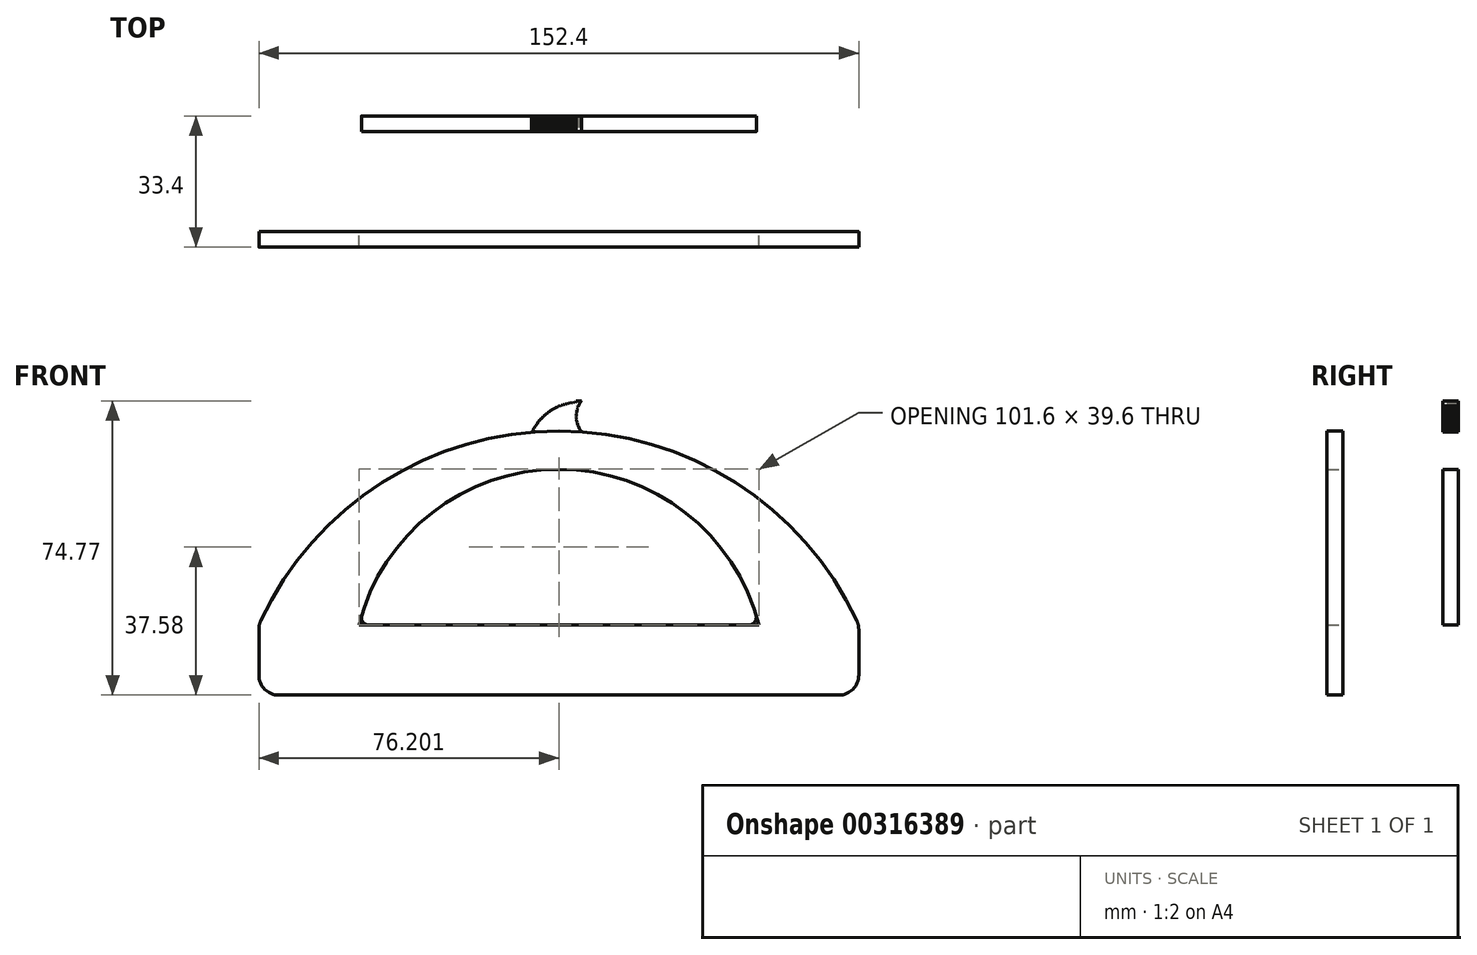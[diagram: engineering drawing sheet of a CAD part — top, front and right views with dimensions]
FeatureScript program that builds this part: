
annotation { "Feature Type Name" : "Feature", "Feature Type Description" : "" }
export const myFeature = defineFeature(function(context is Context, id is Id, definition is map)
    precondition{}
    {
        {
            var Q0;
            Q0=qCreatedBy(makeId("Front.planeOp"),FACE);
            var sketch = newSketch(context, id + "F0", { "sketchPlane" : qUnion([Q0])});
            skLineSegment(sketch, "E0.bottom", {"start": v(-70.76, 0) * mm, "end": v(30.84, 0) * mm});
            skLineSegment(sketch, "E0.top", {"start": v(-70.76, -17.78) * mm, "end": v(30.84, -17.78) * mm});
            skLineSegment(sketch, "E0.left", {"start": v(-70.76, 0) * mm, "end": v(-70.76, -17.78) * mm});
            skLineSegment(sketch, "E0.right", {"start": v(30.84, 0) * mm, "end": v(30.84, -17.78) * mm});
            skLineSegment(sketch, "E1", {"start": v(-19.96, 0) * mm, "end": v(-19.96, 49.32) * mm, "construction": true});
            skLineSegment(sketch, "E2", {"start": v(-70.76, 0) * mm, "end": v(-96.16, 0) * mm});
            skLineSegment(sketch, "E3", {"start": v(30.84, 0) * mm, "end": v(56.24, 0) * mm});
            skLineSegment(sketch, "E4", {"start": v(-96.16, 0) * mm, "end": v(-96.16, -17.78) * mm});
            skLineSegment(sketch, "E5", {"start": v(-96.16, -17.78) * mm, "end": v(-70.76, -17.78) * mm});
            skLineSegment(sketch, "E6", {"start": v(30.84, -17.78) * mm, "end": v(56.24, -17.78) * mm});
            skLineSegment(sketch, "E7", {"start": v(56.24, 0) * mm, "end": v(56.24, -17.78) * mm});
            skArc(sketch, "E8", {"start": v(56.24, 0) * mm, "mid": v(-19.96, 49.32) * mm, "end": v(-96.16, 0) * mm});
            skArc(sketch, "E9", {"start": v(30.84, 0) * mm, "mid": v(-19.96, 39.6) * mm, "end": v(-70.76, 0) * mm});
            skSolve(sketch);
        }
        {
            var Q0;
            Q0=makeQuery(id+"F0.imprint","IMPRINT",FACE,{"disambiguationData":[TD([[makeQuery(id+"F0.imprint","IMPRINT",EDGE,{"derivedFrom":sQuery(id+"F0.wireOp",EDGE,"E2")}),-1.0]])]});
            var Q1;
            Q1=makeQuery(id+"F0.imprint","IMPRINT",FACE,{"disambiguationData":[TD([[makeQuery(id+"F0.imprint","IMPRINT",EDGE,{"derivedFrom":sQuery(id+"F0.wireOp",EDGE,"E0.left")}),-1.0]])]});
            var Q2;
            Q2=makeQuery(id+"F0.imprint","IMPRINT",FACE,{"disambiguationData":[TD([[makeQuery(id+"F0.imprint","IMPRINT",EDGE,{"derivedFrom":sQuery(id+"F0.wireOp",EDGE,"E0.bottom")}),-1.0]])]});
            var Q3;
            Q3=makeQuery(id+"F0.imprint","IMPRINT",FACE,{"disambiguationData":[TD([[makeQuery(id+"F0.imprint","IMPRINT",EDGE,{"derivedFrom":sQuery(id+"F0.wireOp",EDGE,"E0.right")}),1.0]])]});
            extrude(context, id + "F1", {"entities" : qUnion([Q0, Q1, Q2, Q3]), "depth" : 4 * mm});
        }
        {
            var Q0;
            Q0=makeQuery(id+"F1.opExtrude","SWEPT_EDGE",EDGE,{"disambiguationData":[OSD([sQuery(id+"F0.wireOp",EDGE,"E4"),sQuery(id+"F0.wireOp",EDGE,"E5")])]});
            var Q1;
            Q1=makeQuery(id+"F1.opExtrude","SWEPT_EDGE",EDGE,{"disambiguationData":[OSD([sQuery(id+"F0.wireOp",EDGE,"E2"),sQuery(id+"F0.wireOp",EDGE,"E4"),sQuery(id+"F0.wireOp",EDGE,"E8")])]});
            var Q2;
            Q2=makeQuery(id+"F1.opExtrude","SWEPT_EDGE",EDGE,{"disambiguationData":[OSD([sQuery(id+"F0.wireOp",EDGE,"E3"),sQuery(id+"F0.wireOp",EDGE,"E7"),sQuery(id+"F0.wireOp",EDGE,"E8")])]});
            var Q3;
            Q3=makeQuery(id+"F1.opExtrude","SWEPT_EDGE",EDGE,{"disambiguationData":[OSD([sQuery(id+"F0.wireOp",EDGE,"E6"),sQuery(id+"F0.wireOp",EDGE,"E7")])]});
            fillet(context, id + "F2", {"entities" : qUnion([Q0, Q1, Q2, Q3]), "radius" : 5.08 * mm, "tangentPropagation" : true, "allowEdgeOverflow" : false});
        }
        {
            var Q0;
            Q0=makeQuery(id+"F1.opExtrude","CAP_FACE",FACE,{"disambiguationData":[OSD([sQuery(id+"F0.wireOp",EDGE,"E0.bottom"),sQuery(id+"F0.wireOp",EDGE,"E0.top"),sQuery(id+"F0.wireOp",EDGE,"E4"),sQuery(id+"F0.wireOp",EDGE,"E5"),sQuery(id+"F0.wireOp",EDGE,"E6"),sQuery(id+"F0.wireOp",EDGE,"E7"),sQuery(id+"F0.wireOp",EDGE,"E8"),sQuery(id+"F0.wireOp",EDGE,"E9")])],"isStart":true});
            cPlane(context, id + "F3", {"entities" : qUnion([Q0]), "cplaneType" : CPlaneType.OFFSET, "offset" : 25.4 * mm, "width" : 152.4 * mm, "height" : 152.4 * mm});
        }
        {
            var Q0;
            Q0=qCreatedBy(id+"F3.planeOp",FACE);
            var sketch = newSketch(context, id + "F4", { "sketchPlane" : qUnion([Q0])});
            skArc(sketch, "E10.0", {"start": v(-55.77, 1.04) * mm, "mid": v(19.96, 49.32) * mm, "end": v(95.68, 1.04) * mm});
            skArc(sketch, "E11.0", {"start": v(-30.84, 0) * mm, "mid": v(19.96, 39.6) * mm, "end": v(70.76, 0) * mm});
            skLineSegment(sketch, "E12.0", {"start": v(70.76, 0) * mm, "end": v(-30.84, 0) * mm});
            skLineSegment(sketch, "E13.0", {"start": v(91.08, -17.78) * mm, "end": v(-51.16, -17.78) * mm});
            skLineSegment(sketch, "E14.0", {"start": v(-56.24, -1.1) * mm, "end": v(-56.24, -12.7) * mm});
            skArc(sketch, "E15.0", {"start": v(-56.24, -12.7) * mm, "mid": v(-54.75, -16.3) * mm, "end": v(-51.16, -17.78) * mm});
            skArc(sketch, "E16.0", {"start": v(91.08, -17.78) * mm, "mid": v(94.67, -16.3) * mm, "end": v(96.16, -12.7) * mm});
            skLineSegment(sketch, "E17.0", {"start": v(96.16, -1.1) * mm, "end": v(96.16, -12.7) * mm});
            skArc(sketch, "E18.0", {"start": v(-55.77, 1.04) * mm, "mid": v(-56.12, 0) * mm, "end": v(-56.24, -1.1) * mm});
            skArc(sketch, "E19.0", {"start": v(96.16, -1.1) * mm, "mid": v(96.04, 0) * mm, "end": v(95.68, 1.04) * mm});
            skArc(sketch, "E20", {"start": v(26.92, 49.02) * mm, "mid": v(21.7, 54.8) * mm, "end": v(14.23, 57) * mm});
            skArc(sketch, "E21", {"start": v(14.23, 49.12) * mm, "mid": v(15.42, 53.06) * mm, "end": v(14.23, 57) * mm});
            skLineSegment(sketch, "E22", {"start": v(26.34, 50.08) * mm, "end": v(26.1, 50.14) * mm});
            skLineSegment(sketch, "E23", {"start": v(26.1, 50.14) * mm, "end": v(26.15, 50.38) * mm});
            skLineSegment(sketch, "E24", {"start": v(26.15, 50.38) * mm, "end": v(25.9, 50.46) * mm});
            skLineSegment(sketch, "E25", {"start": v(25.9, 50.46) * mm, "end": v(25.9, 50.75) * mm});
            skLineSegment(sketch, "E26", {"start": v(25.9, 50.75) * mm, "end": v(25.67, 50.81) * mm});
            skLineSegment(sketch, "E27", {"start": v(25.67, 50.81) * mm, "end": v(25.67, 51.08) * mm});
            skLineSegment(sketch, "E28", {"start": v(25.67, 51.08) * mm, "end": v(25.41, 51.16) * mm});
            skLineSegment(sketch, "E29", {"start": v(25.41, 51.16) * mm, "end": v(25.41, 51.43) * mm});
            skLineSegment(sketch, "E30", {"start": v(25.41, 51.43) * mm, "end": v(25.2, 51.5) * mm});
            skLineSegment(sketch, "E31", {"start": v(25.2, 51.5) * mm, "end": v(25.2, 51.7) * mm});
            skLineSegment(sketch, "E32", {"start": v(25.2, 51.7) * mm, "end": v(25, 51.77) * mm});
            skLineSegment(sketch, "E33", {"start": v(25, 51.77) * mm, "end": v(25, 51.94) * mm});
            skLineSegment(sketch, "E34", {"start": v(23.63, 53.2) * mm, "end": v(23.56, 53.4) * mm});
            skLineSegment(sketch, "E35", {"start": v(23.56, 53.4) * mm, "end": v(23.32, 53.44) * mm});
            skLineSegment(sketch, "E36", {"start": v(23.32, 53.44) * mm, "end": v(23.29, 53.64) * mm});
            skLineSegment(sketch, "E37", {"start": v(23.29, 53.64) * mm, "end": v(23.07, 53.64) * mm});
            skLineSegment(sketch, "E38", {"start": v(23.07, 53.64) * mm, "end": v(23, 53.87) * mm});
            skLineSegment(sketch, "E39", {"start": v(23, 53.87) * mm, "end": v(22.78, 53.85) * mm});
            skLineSegment(sketch, "E40", {"start": v(22.78, 53.85) * mm, "end": v(22.77, 54.06) * mm});
            skLineSegment(sketch, "E41", {"start": v(22.77, 54.06) * mm, "end": v(22.5, 54.06) * mm});
            skLineSegment(sketch, "E42", {"start": v(22.5, 54.06) * mm, "end": v(22.48, 54.27) * mm});
            skLineSegment(sketch, "E43", {"start": v(22.48, 54.27) * mm, "end": v(22.28, 54.22) * mm});
            skLineSegment(sketch, "E44", {"start": v(22.28, 54.22) * mm, "end": v(22.23, 54.43) * mm});
            skLineSegment(sketch, "E45", {"start": v(22.23, 54.43) * mm, "end": v(22, 54.42) * mm});
            skLineSegment(sketch, "E46", {"start": v(22, 54.42) * mm, "end": v(21.94, 54.62) * mm});
            skLineSegment(sketch, "E47", {"start": v(21.94, 54.62) * mm, "end": v(21.75, 54.6) * mm});
            skLineSegment(sketch, "E48", {"start": v(21.75, 54.6) * mm, "end": v(21.67, 54.8) * mm});
            skLineSegment(sketch, "E49", {"start": v(21.67, 54.8) * mm, "end": v(21.5, 54.73) * mm});
            skLineSegment(sketch, "E50", {"start": v(21.5, 54.73) * mm, "end": v(21.47, 54.94) * mm});
            skLineSegment(sketch, "E51", {"start": v(21.47, 54.94) * mm, "end": v(21.3, 54.85) * mm});
            skLineSegment(sketch, "E52", {"start": v(21.3, 54.85) * mm, "end": v(21.22, 55.05) * mm});
            skLineSegment(sketch, "E53", {"start": v(21.22, 55.05) * mm, "end": v(21.01, 55.02) * mm});
            skLineSegment(sketch, "E54", {"start": v(21.01, 55.02) * mm, "end": v(20.98, 55.2) * mm});
            skLineSegment(sketch, "E55", {"start": v(20.98, 55.2) * mm, "end": v(20.77, 55.18) * mm});
            skLineSegment(sketch, "E56", {"start": v(20.77, 55.18) * mm, "end": v(20.7, 55.34) * mm});
            skLineSegment(sketch, "E57", {"start": v(20.7, 55.34) * mm, "end": v(20.5, 55.3) * mm});
            skLineSegment(sketch, "E58", {"start": v(20.5, 55.3) * mm, "end": v(20.36, 55.5) * mm});
            skLineSegment(sketch, "E59", {"start": v(20.36, 55.5) * mm, "end": v(20.2, 55.44) * mm});
            skLineSegment(sketch, "E60", {"start": v(20.2, 55.44) * mm, "end": v(20.1, 55.63) * mm});
            skLineSegment(sketch, "E61", {"start": v(20.1, 55.63) * mm, "end": v(19.89, 55.57) * mm});
            skLineSegment(sketch, "E62", {"start": v(19.89, 55.57) * mm, "end": v(19.7, 55.8) * mm});
            skLineSegment(sketch, "E63", {"start": v(19.7, 55.8) * mm, "end": v(19.47, 55.7) * mm});
            skLineSegment(sketch, "E64", {"start": v(19.47, 55.7) * mm, "end": v(19.39, 55.94) * mm});
            skLineSegment(sketch, "E65", {"start": v(19.39, 55.94) * mm, "end": v(19.19, 55.85) * mm});
            skLineSegment(sketch, "E66", {"start": v(19.19, 55.85) * mm, "end": v(18.96, 56.06) * mm});
            skLineSegment(sketch, "E67", {"start": v(18.96, 56.06) * mm, "end": v(18.76, 55.94) * mm});
            skLineSegment(sketch, "E68", {"start": v(18.76, 55.94) * mm, "end": v(18.5, 56.2) * mm});
            skLineSegment(sketch, "E69", {"start": v(18.5, 56.2) * mm, "end": v(18.24, 56.02) * mm});
            skLineSegment(sketch, "E70", {"start": v(18.24, 56.02) * mm, "end": v(18, 56.37) * mm});
            skLineSegment(sketch, "E71", {"start": v(18, 56.37) * mm, "end": v(17.7, 56.24) * mm});
            skLineSegment(sketch, "E72", {"start": v(17.7, 56.24) * mm, "end": v(17.56, 56.48) * mm});
            skLineSegment(sketch, "E73", {"start": v(17.56, 56.48) * mm, "end": v(17.34, 56.3) * mm});
            skLineSegment(sketch, "E74", {"start": v(17.34, 56.3) * mm, "end": v(17.03, 56.54) * mm});
            skLineSegment(sketch, "E75", {"start": v(17.03, 56.54) * mm, "end": v(16.8, 56.36) * mm});
            skLineSegment(sketch, "E76", {"start": v(16.8, 56.36) * mm, "end": v(16.57, 56.65) * mm});
            skLineSegment(sketch, "E77", {"start": v(16.57, 56.65) * mm, "end": v(16.32, 56.42) * mm});
            skLineSegment(sketch, "E78", {"start": v(16.32, 56.42) * mm, "end": v(16.09, 56.7) * mm});
            skLineSegment(sketch, "E79", {"start": v(16.09, 56.7) * mm, "end": v(15.9, 56.46) * mm});
            skLineSegment(sketch, "E80", {"start": v(15.9, 56.46) * mm, "end": v(15.68, 56.73) * mm});
            skLineSegment(sketch, "E81", {"start": v(26.34, 50.08) * mm, "end": v(26.27, 49.8) * mm});
            skLineSegment(sketch, "E82", {"start": v(26.27, 49.8) * mm, "end": v(26.5, 49.7) * mm});
            skLineSegment(sketch, "E83", {"start": v(26.5, 49.7) * mm, "end": v(26.41, 49.5) * mm});
            skLineSegment(sketch, "E84", {"start": v(26.41, 49.5) * mm, "end": v(26.72, 49.4) * mm});
            skLineSegment(sketch, "E85", {"start": v(26.72, 49.4) * mm, "end": v(26.6, 49.2) * mm});
            skLineSegment(sketch, "E86", {"start": v(26.6, 49.2) * mm, "end": v(26.85, 49.15) * mm});
            skLineSegment(sketch, "E87", {"start": v(25, 51.94) * mm, "end": v(24.79, 51.94) * mm});
            skLineSegment(sketch, "E88", {"start": v(24.79, 51.94) * mm, "end": v(24.79, 52.18) * mm});
            skLineSegment(sketch, "E89", {"start": v(24.79, 52.18) * mm, "end": v(24.53, 52.22) * mm});
            skLineSegment(sketch, "E90", {"start": v(24.53, 52.22) * mm, "end": v(24.52, 52.47) * mm});
            skLineSegment(sketch, "E91", {"start": v(24.52, 52.47) * mm, "end": v(24.24, 52.51) * mm});
            skLineSegment(sketch, "E92", {"start": v(24.24, 52.51) * mm, "end": v(24.24, 52.77) * mm});
            skLineSegment(sketch, "E93", {"start": v(24.24, 52.77) * mm, "end": v(23.94, 52.77) * mm});
            skLineSegment(sketch, "E94", {"start": v(23.94, 52.77) * mm, "end": v(23.92, 53.08) * mm});
            skLineSegment(sketch, "E95", {"start": v(15.68, 56.73) * mm, "end": v(15.53, 56.92) * mm});
            skLineSegment(sketch, "E96", {"start": v(14.9, 55.71) * mm, "end": v(15.3, 55.46) * mm});
            skLineSegment(sketch, "E97", {"start": v(15.3, 55.46) * mm, "end": v(15.1, 55.15) * mm});
            skLineSegment(sketch, "E98", {"start": v(15.1, 55.15) * mm, "end": v(15.4, 54.8) * mm});
            skLineSegment(sketch, "E99", {"start": v(15.42, 54.75) * mm, "end": v(15.27, 54.49) * mm});
            skLineSegment(sketch, "E100", {"start": v(15.26, 54.45) * mm, "end": v(15.48, 54.18) * mm});
            skLineSegment(sketch, "E101", {"start": v(15.48, 54.18) * mm, "end": v(15.36, 53.95) * mm});
            skLineSegment(sketch, "E102", {"start": v(15.36, 53.95) * mm, "end": v(15.55, 53.72) * mm});
            skLineSegment(sketch, "E103", {"start": v(15.55, 53.72) * mm, "end": v(15.4, 53.5) * mm});
            skLineSegment(sketch, "E104", {"start": v(15.4, 54.8) * mm, "end": v(15.42, 54.75) * mm});
            skLineSegment(sketch, "E105", {"start": v(15.4, 53.5) * mm, "end": v(15.55, 53.24) * mm});
            skLineSegment(sketch, "E106", {"start": v(15.55, 53.24) * mm, "end": v(15.42, 53.04) * mm});
            skLineSegment(sketch, "E107", {"start": v(15.42, 53.04) * mm, "end": v(15.61, 52.91) * mm});
            skLineSegment(sketch, "E108", {"start": v(15.61, 52.91) * mm, "end": v(15.4, 52.72) * mm});
            skLineSegment(sketch, "E109", {"start": v(15.4, 52.72) * mm, "end": v(15.59, 52.53) * mm});
            skLineSegment(sketch, "E110", {"start": v(15.59, 52.53) * mm, "end": v(15.4, 52.36) * mm});
            skLineSegment(sketch, "E111", {"start": v(15.4, 52.36) * mm, "end": v(15.54, 52.23) * mm});
            skLineSegment(sketch, "E112", {"start": v(15.54, 52.23) * mm, "end": v(15.4, 52.1) * mm});
            skLineSegment(sketch, "E113", {"start": v(15.4, 52.1) * mm, "end": v(15.5, 51.84) * mm});
            skLineSegment(sketch, "E114", {"start": v(15.5, 51.84) * mm, "end": v(15.3, 51.78) * mm});
            skLineSegment(sketch, "E115", {"start": v(15.3, 51.78) * mm, "end": v(15.38, 51.54) * mm});
            skLineSegment(sketch, "E116", {"start": v(15.38, 51.54) * mm, "end": v(15.24, 51.5) * mm});
            skLineSegment(sketch, "E117", {"start": v(15.24, 51.5) * mm, "end": v(15.32, 51.26) * mm});
            skLineSegment(sketch, "E118", {"start": v(15.32, 51.26) * mm, "end": v(15.17, 51.21) * mm});
            skLineSegment(sketch, "E119", {"start": v(15.17, 51.21) * mm, "end": v(15.25, 50.98) * mm});
            skLineSegment(sketch, "E120", {"start": v(15.25, 50.98) * mm, "end": v(15.1, 50.92) * mm});
            skLineSegment(sketch, "E121", {"start": v(15.1, 50.92) * mm, "end": v(15.16, 50.72) * mm});
            skLineSegment(sketch, "E122", {"start": v(15.16, 50.72) * mm, "end": v(15, 50.66) * mm});
            skLineSegment(sketch, "E123", {"start": v(15, 50.66) * mm, "end": v(15.07, 50.48) * mm});
            skLineSegment(sketch, "E124", {"start": v(15.07, 50.48) * mm, "end": v(14.94, 50.48) * mm});
            skLineSegment(sketch, "E125", {"start": v(14.94, 50.48) * mm, "end": v(14.94, 50.3) * mm});
            skLineSegment(sketch, "E126", {"start": v(14.94, 50.3) * mm, "end": v(14.86, 50.3) * mm});
            skLineSegment(sketch, "E127", {"start": v(14.86, 50.3) * mm, "end": v(14.86, 50.13) * mm});
            skLineSegment(sketch, "E128", {"start": v(14.86, 50.13) * mm, "end": v(14.78, 50.1) * mm});
            skLineSegment(sketch, "E129", {"start": v(14.78, 50.1) * mm, "end": v(14.78, 49.93) * mm});
            skLineSegment(sketch, "E130", {"start": v(14.78, 49.93) * mm, "end": v(14.68, 49.9) * mm});
            skLineSegment(sketch, "E131", {"start": v(14.68, 49.9) * mm, "end": v(14.73, 49.77) * mm});
            skLineSegment(sketch, "E132", {"start": v(14.73, 49.77) * mm, "end": v(14.59, 49.72) * mm});
            skLineSegment(sketch, "E133", {"start": v(23.63, 53.2) * mm, "end": v(23.92, 53.08) * mm});
            skSolve(sketch);
        }
        {
            var Q0;
            Q0=makeQuery(id+"F4.imprint","IMPRINT",FACE,{"disambiguationData":[TD([[makeQuery(id+"F4.imprint","IMPRINT",EDGE,{"derivedFrom":sQuery(id+"F4.wireOp",EDGE,"E11.0")}),1.0]])]});
            extrude(context, id + "F5", {"entities" : qUnion([Q0]), "depth" : 4 * mm});
        }
        {
            var Q0;
            Q0=makeQuery(id+"F4.imprint","IMPRINT",FACE,{"disambiguationData":[TD([[makeQuery(id+"F4.imprint","IMPRINT",EDGE,{"derivedFrom":sQuery(id+"F4.wireOp",EDGE,"E22")}),1.0]])]});
            extrude(context, id + "F6", {"entities" : qUnion([Q0]), "depth" : 4 * mm});
        }
        {
            var Q0;
            {var subQ0=sQuery(id+"F4.wireOp",EDGE,"E12.0");var subQ1=sQuery(id+"F4.wireOp",EDGE,"E11.0");Q0=makeQuery(id+"F5.opExtrude","SWEPT_EDGE",EDGE,{"disambiguationData":[OSD([subQ1,subQ0]),TDD([makeQuery(id+"F4.imprint","INTERSECT",VERTEX,{"disambiguationData":[OD(0.0)],"derivedFrom":[subQ1,subQ0]})])]});}
            var Q1;
            {var subQ0=sQuery(id+"F4.wireOp",EDGE,"E12.0");var subQ1=sQuery(id+"F4.wireOp",EDGE,"E11.0");Q1=makeQuery(id+"F5.opExtrude","SWEPT_EDGE",EDGE,{"disambiguationData":[OSD([subQ1,subQ0]),TDD([makeQuery(id+"F4.imprint","INTERSECT",VERTEX,{"disambiguationData":[OD(1.0)],"derivedFrom":[subQ1,subQ0]})])]});}
            fillet(context, id + "F7", {"entities" : qUnion([Q0, Q1]), "radius" : 2 * mm, "tangentPropagation" : true, "allowEdgeOverflow" : false});
        }
    });
